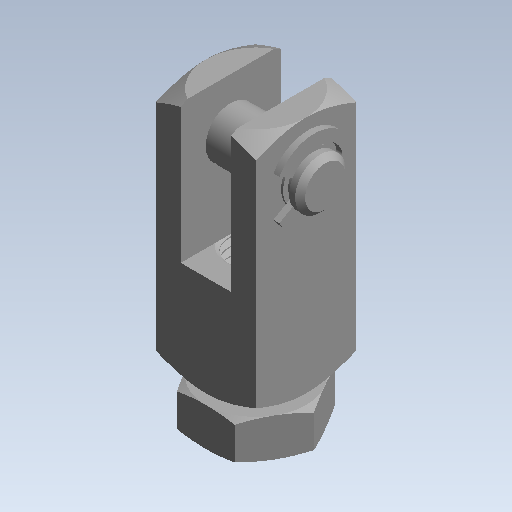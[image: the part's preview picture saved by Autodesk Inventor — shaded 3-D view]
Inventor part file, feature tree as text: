
AUTODESK INVENTOR PART (.ipt)
format: ipt  version: 2020 (Build 240168000, 168)  size: 711,168 bytes
history: native  units: mm (DEFAULTED — no unit token found)
features: other x3, revolve x1, mirror x1
ambient origin geometry x8: Origin, YZ Plane, XZ Plane, XY Plane, X Axis, Y Axis, Z Axis, Center Point
bodies: Solid1 (feature_tree), Solid2 (feature_tree), Solid3 (feature_tree), Solid4 (feature_tree), Solid5 (feature_tree)
feature tree (5):
  other  "Cut-Revolve4"
  revolve  "Revolve3"  [1 undecoded]
  other  "Cut-Extrude13[1]"
  other  "Boss-Extrude1"
  mirror  "Mirror1"
note: 1 required parameter value undecoded (feature->parameter linkage not recoverable at this tier; creation-order binding heuristic only, values carry confidence <= 0.55)
